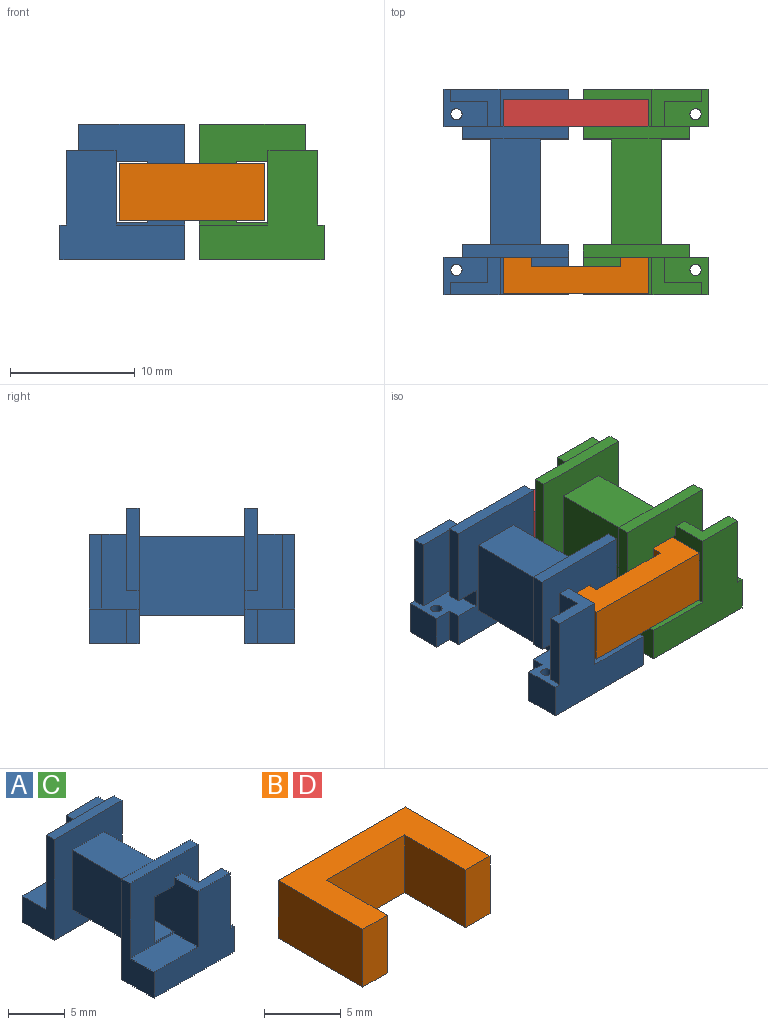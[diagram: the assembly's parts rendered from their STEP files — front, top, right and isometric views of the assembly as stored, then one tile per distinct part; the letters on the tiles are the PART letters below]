
ASSEMBLY  parts=4 mates=3
PART A: 44 faces, bbox 10x16.5x10.9 mm
  f0: plane 8.5x8.1mm, normal (0,-1,0), area 47.6mm2, adj f13,f14,f15,f16,f17,f18,f20,f31
  f1: plane 2.8x1mm, normal (1,0,0), area 2.8mm2, adj f4,f8,f19,f29
  f2: plane 6.6x1mm, normal (1,0,0), area 6.6mm2, adj f3,f5,f21,f42
  f3: plane 8.5x8.1mm, normal (0,1,0), area 47.6mm2, adj f2,f7,f13,f14,f15,f16,f21,f24
  f4: plane 10.9x8.5mm, normal (0,1,0), area 64mm2, adj f1,f8,f9,f10,f11,f12,f17,f18
  f5: plane 10.9x8.5mm, normal (0,-1,0), area 64mm2, adj f2,f6,f7,f9,f10,f11,f12,f21
  f6: plane 4x3.5mm, normal (0,0,1), area 8.9mm2, adj f5,f7,f22,f25,f27,f28,f38,f39
  f7: plane 6x3mm, normal (1,0,0), area 13.5mm2, adj f3,f5,f6,f37,f38,f42
  f8: plane 4x3.5mm, normal (0,0,1), area 8.9mm2, adj f1,f4,f29,f30,f32,f33,f35,f36
  f9: plane 8.5x6.4mm, normal (-1,0,0), area 54.4mm2, adj f4,f5,f10,f12
  f10: plane 8.5x4mm, normal (0,0,-1), area 34mm2, adj f4,f5,f9,f11
  f11: plane 8.5x6.4mm, normal (1,0,0), area 54.4mm2, adj f4,f5,f10,f12
  f12: plane 8.5x4mm, normal (0,0,1), area 34mm2, adj f4,f5,f9,f11
  f13: plane 10.5x4.9mm, normal (1,0,0), area 51.5mm2, adj f0,f3,f14,f16
  f14: plane 10.5x2.5mm, normal (0,0,-1), area 26.2mm2, adj f0,f3,f13,f15
  f15: plane 16.5x6mm, normal (-1,0,0), area 87.5mm2, adj f0,f3,f14,f16,f26,f27,f30,f31
  f16: plane 10.5x2.5mm, normal (0,0,1), area 26.2mm2, adj f0,f3,f13,f15
  f17: plane 8.5x1mm, normal (0,0,1), area 8.5mm2, adj f0,f4,f18,f20
  f18: plane 10.9x4mm, normal (-1,0,0), area 19.3mm2, adj f0,f4,f17,f19,f30,f31
  f19: plane 10x4mm, normal (0,0,-1), area 37.9mm2, adj f1,f4,f18,f29,f30,f32,f41
  f20: plane 6.6x1mm, normal (1,0,0), area 6.6mm2, adj f0,f4,f17,f43
  f21: plane 8.5x1mm, normal (0,0,1), area 8.5mm2, adj f2,f3,f5,f24
  f22: plane 2.8x1mm, normal (1,0,0), area 2.8mm2, adj f5,f6,f23,f25
  f23: plane 10x4mm, normal (0,0,-1), area 37.9mm2, adj f5,f22,f24,f25,f27,f28,f40
  f24: plane 10.9x4mm, normal (-1,0,0), area 19.3mm2, adj f3,f5,f21,f23,f26,f27
  f25: plane 2.8x1.5mm, normal (0,-1,0), area 4.2mm2, adj f6,f22,f23,f28
  f26: plane 5.5x3mm, normal (0,0,1), area 16.5mm2, adj f3,f15,f24,f27
  f27: plane 10x8.8mm, normal (0,1,0), area 52mm2, adj f6,f15,f23,f24,f26,f28,f37,f39
  f28: plane 3x2.8mm, normal (1,0,0), area 8.4mm2, adj f6,f23,f25,f27
  f29: plane 2.8x1.5mm, normal (0,1,0), area 4.2mm2, adj f1,f8,f19,f32
  f30: plane 10x8.8mm, normal (0,-1,0), area 52mm2, adj f8,f15,f18,f19,f31,f32,f34,f36
  f31: plane 5.5x3mm, normal (0,0,1), area 16.5mm2, adj f0,f15,f18,f30
  f32: plane 3x2.8mm, normal (1,0,0), area 8.4mm2, adj f8,f19,f29,f30
  f33: plane 6x3mm, normal (1,0,0), area 13.5mm2, adj f0,f4,f8,f34,f35,f43
  f34: plane 4x3mm, normal (0,0,1), area 6mm2, adj f0,f15,f30,f33,f35,f36
  f35: plane 6x3mm, normal (0,1,0), area 18mm2, adj f8,f33,f34,f36
  f36: plane 6x1mm, normal (1,0,0), area 6mm2, adj f8,f30,f34,f35
  f37: plane 4x3mm, normal (0,0,1), area 6mm2, adj f3,f7,f15,f27,f38,f39
  f38: plane 6x3mm, normal (0,-1,0), area 18mm2, adj f6,f7,f37,f39
  f39: plane 6x1mm, normal (1,0,0), area 6mm2, adj f6,f27,f37,f38
  f40: cylinder r=0.45mm len=2.8mm, axis (0,0,1), area 7.9mm2, adj f6,f23
  f41: cylinder r=0.45mm len=2.8mm, axis (0,0,1), area 7.9mm2, adj f8,f19
  f42: plane 2x1mm, normal (0,0,-1), area 2mm2, adj f2,f3,f5,f7
  f43: plane 2x1mm, normal (0,0,-1), area 2mm2, adj f0,f4,f20,f33
PART B: 10 faces, bbox 11.7x7.8x4.6 mm
  f0: plane 7.8x4.6mm, normal (-1,0,0), area 35.9mm2, adj f1,f7,f8,f9
  f1: plane 4.6x2.25mm, normal (0,-1,0), area 10.3mm2, adj f0,f2,f8,f9
  f2: plane 5.6x4.6mm, normal (1,0,0), area 25.8mm2, adj f1,f3,f8,f9
  f3: plane 7.2x4.6mm, normal (0,-1,0), area 33.1mm2, adj f2,f4,f8,f9
  f4: plane 5.6x4.6mm, normal (-1,0,0), area 25.8mm2, adj f3,f5,f8,f9
  f5: plane 4.6x2.25mm, normal (0,-1,0), area 10.4mm2, adj f4,f6,f8,f9
  f6: plane 7.8x4.6mm, normal (1,0,0), area 35.9mm2, adj f5,f7,f8,f9
  f7: plane 11.7x4.6mm, normal (0,1,0), area 53.8mm2, adj f0,f6,f8,f9
  f8: plane 11.7x7.8mm, normal (0,0,1), area 50.9mm2, adj f0,f1,f2,f3,f4,f5,f6,f7
  f9: plane 11.7x7.8mm, normal (0,0,-1), area 50.9mm2, adj f0,f1,f2,f3,f4,f5,f6,f7
PART C: same geometry as A
PART D: same geometry as B
PLACE A rot(axis=(0,0,1),180deg) t=(0.24,13,0.9)mm
PLACE B rot(axis=(0,0,1),180deg) t=(8.94,7.4,1.8)mm
PLACE C t=(5.94,2.5,0.9)mm fixed
PLACE D t=(-2.76,7.4,1.8)mm
MATE fastened A.f0 <-> D.f3  axis (0,1,0) through (-0.51,13,4.1)mm
MATE fastened D.f3 <-> C.f3  axis (0,-1,0) through (6.69,13,4.1)mm
MATE fastened B.f1 <-> D.f5  axis (0,1,0) through (7.81,7.4,4.1)mm
